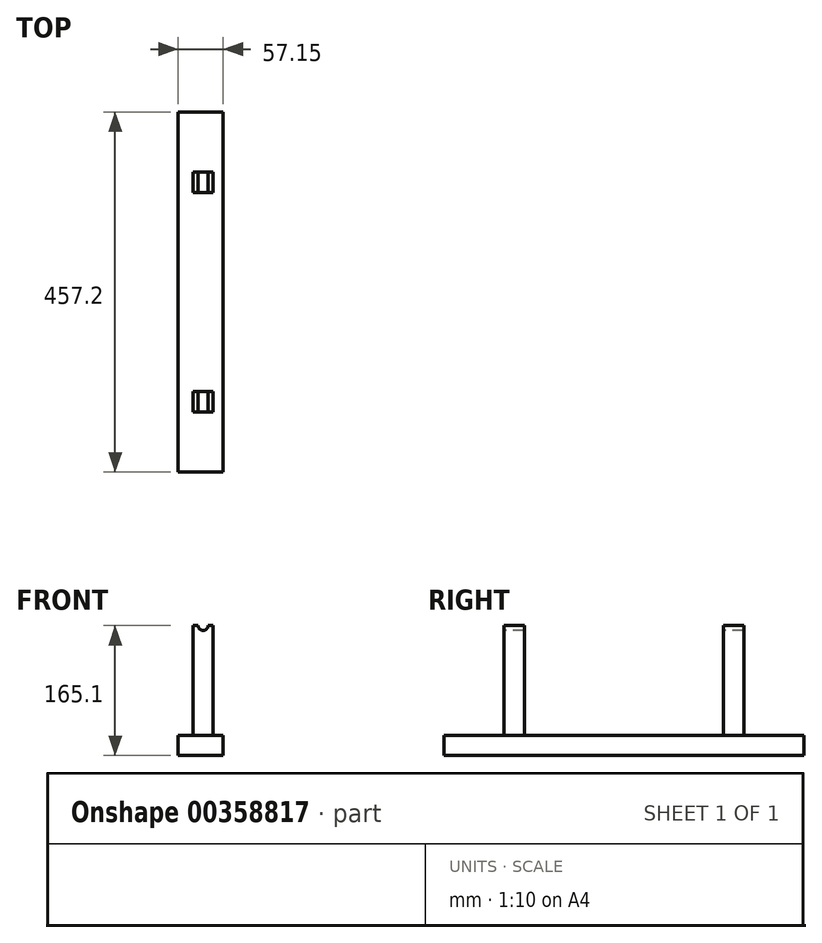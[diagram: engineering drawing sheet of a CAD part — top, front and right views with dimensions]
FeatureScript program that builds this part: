
annotation { "Feature Type Name" : "Feature", "Feature Type Description" : "" }
export const myFeature = defineFeature(function(context is Context, id is Id, definition is map)
    precondition{}
    {
        {
            var Q0;
            Q0=qCreatedBy(makeId("Right.planeOp"),FACE);
            var sketch = newSketch(context, id + "F0", { "sketchPlane" : qUnion([Q0])});
            skLineSegment(sketch, "E0.bottom", {"start": v(0, 0) * mm, "end": v(457.2, 0) * mm});
            skLineSegment(sketch, "E0.top", {"start": v(0, 25.4) * mm, "end": v(457.2, 25.4) * mm});
            skLineSegment(sketch, "E0.left", {"start": v(0, 0) * mm, "end": v(0, 25.4) * mm});
            skLineSegment(sketch, "E0.right", {"start": v(457.2, 0) * mm, "end": v(457.2, 25.4) * mm});
            skSolve(sketch);
        }
        {
            var Q0;
            Q0=qSketchRegion(id+"F0",true);
            extrude(context, id + "F1", {"entities" : qUnion([Q0]), "oppositeDirection" : true, "depth" : 203.2 * mm});
        }
        {
            var Q0;
            Q0=makeQuery(id+"F1.opExtrude","CAP_FACE",FACE,{"disambiguationData":[OSD([sQuery(id+"F0.wireOp",EDGE,"E0.bottom"),sQuery(id+"F0.wireOp",EDGE,"E0.top"),sQuery(id+"F0.wireOp",EDGE,"E0.left"),sQuery(id+"F0.wireOp",EDGE,"E0.right")])],"isStart":true});
            var sketch = newSketch(context, id + "F2", { "sketchPlane" : qUnion([Q0])});
            skLineSegment(sketch, "E1.bottom", {"start": v(76.2, 25.4) * mm, "end": v(102.38, 25.4) * mm});
            skLineSegment(sketch, "E1.top", {"start": v(76.2, 165.1) * mm, "end": v(102.38, 165.1) * mm});
            skLineSegment(sketch, "E1.left", {"start": v(76.2, 25.4) * mm, "end": v(76.2, 165.1) * mm});
            skLineSegment(sketch, "E1.right", {"start": v(102.38, 25.4) * mm, "end": v(102.38, 165.1) * mm});
            skLineSegment(sketch, "E2", {"start": v(228.6, 68.14) * mm, "end": v(228.6, -33.61) * mm});
            skPoint(sketch, "E2.startSnap0", {"position": v(228.6, 25.4) * mm});
            skLineSegment(sketch, "E3.MirrorCS", {"start": v(381, 25.4) * mm, "end": v(381, 165.1) * mm});
            skLineSegment(sketch, "E4.MirrorCS", {"start": v(381, 25.4) * mm, "end": v(354.82, 25.4) * mm});
            skLineSegment(sketch, "E5.MirrorCS", {"start": v(354.82, 25.4) * mm, "end": v(354.82, 165.1) * mm});
            skLineSegment(sketch, "E6.MirrorCS", {"start": v(381, 165.1) * mm, "end": v(354.82, 165.1) * mm});
            skSolve(sketch);
        }
        {
            var Q0;
            Q0=qSketchRegion(id+"F2",true);
            extrude(context, id + "F3", {"entities" : qUnion([Q0]), "oppositeDirection" : true, "depth" : 38.1 * mm});
        }
        {
            var Q0;
            Q0=makeQuery(id+"F3.opExtrude","SWEPT_FACE",FACE,{"disambiguationData":[OSD([sQuery(id+"F2.wireOp",EDGE,"E1.left")])]});
            var sketch = newSketch(context, id + "F4", { "sketchPlane" : qUnion([Q0])});
            skLineSegment(sketch, "E7.bottom", {"start": v(0, 25.4) * mm, "end": v(-12.7, 25.4) * mm});
            skLineSegment(sketch, "E7.top", {"start": v(0, 165.1) * mm, "end": v(-12.7, 165.1) * mm});
            skLineSegment(sketch, "E7.left", {"start": v(0, 25.4) * mm, "end": v(0, 165.1) * mm});
            skLineSegment(sketch, "E7.right", {"start": v(-12.7, 25.4) * mm, "end": v(-12.7, 165.1) * mm});
            skSolve(sketch);
        }
        {
            var Q0;
            Q0=qSketchRegion(id+"F4",true);
            extrude(context, id + "F5", {"entities" : qUnion([Q0]), "operationType" : NewBodyOperationType.REMOVE, "endBound" : BoundingType.THROUGH_ALL, "oppositeDirection" : true, "depth" : 25.4 * mm});
        }
        {
            var Q0;
            Q0=makeQuery(id+"F1.opExtrude","CAP_FACE",FACE,{"disambiguationData":[OSD([sQuery(id+"F0.wireOp",EDGE,"E0.bottom"),sQuery(id+"F0.wireOp",EDGE,"E0.top"),sQuery(id+"F0.wireOp",EDGE,"E0.left"),sQuery(id+"F0.wireOp",EDGE,"E0.right")])],"isStart":false});
            var sketch = newSketch(context, id + "F6", { "sketchPlane" : qUnion([Q0])});
            skLineSegment(sketch, "E8.bottom", {"start": v(-331.33, 25.4) * mm, "end": v(-299.58, 25.4) * mm});
            skLineSegment(sketch, "E8.top", {"start": v(-331.33, 177.8) * mm, "end": v(-299.58, 177.8) * mm});
            skLineSegment(sketch, "E8.left", {"start": v(-331.33, 25.4) * mm, "end": v(-331.33, 177.8) * mm});
            skLineSegment(sketch, "E8.right", {"start": v(-299.58, 25.4) * mm, "end": v(-299.58, 177.8) * mm});
            skLineSegment(sketch, "E9.bottom", {"start": v(-172.58, 25.4) * mm, "end": v(-140.83, 25.4) * mm});
            skLineSegment(sketch, "E9.top", {"start": v(-172.58, 177.8) * mm, "end": v(-140.83, 177.8) * mm});
            skLineSegment(sketch, "E9.left", {"start": v(-172.58, 25.4) * mm, "end": v(-172.58, 177.8) * mm});
            skLineSegment(sketch, "E9.right", {"start": v(-140.83, 25.4) * mm, "end": v(-140.83, 177.8) * mm});
            skSolve(sketch);
        }
        {
            var Q0;
            Q0=qSketchRegion(id+"F6",true);
            extrude(context, id + "F7", {"entities" : qUnion([Q0]), "operationType" : NewBodyOperationType.ADD, "oppositeDirection" : true, "depth" : 38.1 * mm});
        }
        {
            var Q0;
            Q0=makeQuery(id+"F7.opExtrude","SWEPT_FACE",FACE,{"disambiguationData":[OSD([sQuery(id+"F6.wireOp",EDGE,"E8.left")])]});
            var sketch = newSketch(context, id + "F8", { "sketchPlane" : qUnion([Q0])});
            skPoint(sketch, "E10", {"position": v(184.15, 165.1) * mm});
            skPoint(sketch, "E10.positionSnap0", {"position": v(184.15, 177.8) * mm});
            skCircle(sketch, "E11.cCircle", {"center": v(184.15, 165.1) * mm, "radius": 25.4 * mm, "construction": true});
            skLineSegment(sketch, "E11.0", {"start": v(169.49, 190.5) * mm, "end": v(198.81, 190.5) * mm});
            skLineSegment(sketch, "E11.1", {"start": v(198.81, 190.5) * mm, "end": v(213.48, 165.1) * mm});
            skLineSegment(sketch, "E11.2", {"start": v(213.48, 165.1) * mm, "end": v(198.81, 139.7) * mm});
            skLineSegment(sketch, "E11.3", {"start": v(198.81, 139.7) * mm, "end": v(169.49, 139.7) * mm});
            skLineSegment(sketch, "E11.4", {"start": v(169.49, 139.7) * mm, "end": v(154.82, 165.1) * mm});
            skLineSegment(sketch, "E11.5", {"start": v(154.82, 165.1) * mm, "end": v(169.49, 190.5) * mm});
            skPoint(sketch, "E11.0.midPoint", {"position": v(184.15, 190.5) * mm});
            skSolve(sketch);
        }
        {
            var Q0;
            Q0=qSketchRegion(id+"F8",true);
            extrude(context, id + "F9", {"entities" : qUnion([Q0]), "operationType" : NewBodyOperationType.ADD, "oppositeDirection" : true, "depth" : 196.85 * mm, "hasSecondDirection" : true, "secondDirectionOppositeDirection" : false, "secondDirectionDepth" : 6.35 * mm});
        }
        {
            var Q0;
            Q0=makeQuery(id+"F7.boolean.opBoolean","MERGE",FACE,{"derivedFrom":[makeQuery(id+"F1.opExtrude","CAP_FACE",FACE,{"disambiguationData":[OSD([sQuery(id+"F0.wireOp",EDGE,"E0.bottom"),sQuery(id+"F0.wireOp",EDGE,"E0.top"),sQuery(id+"F0.wireOp",EDGE,"E0.left"),sQuery(id+"F0.wireOp",EDGE,"E0.right")])],"isStart":false}),makeQuery(id+"F7.opExtrude","CAP_FACE",FACE,{"disambiguationData":[OSD([sQuery(id+"F6.wireOp",EDGE,"E8.bottom"),sQuery(id+"F6.wireOp",EDGE,"E8.top"),sQuery(id+"F6.wireOp",EDGE,"E8.left"),sQuery(id+"F6.wireOp",EDGE,"E8.right")])],"isStart":true}),makeQuery(id+"F7.opExtrude","CAP_FACE",FACE,{"disambiguationData":[OSD([sQuery(id+"F6.wireOp",EDGE,"E9.bottom"),sQuery(id+"F6.wireOp",EDGE,"E9.top"),sQuery(id+"F6.wireOp",EDGE,"E9.left"),sQuery(id+"F6.wireOp",EDGE,"E9.right")])],"isStart":true})]});
            var sketch = newSketch(context, id + "F10", { "sketchPlane" : qUnion([Q0])});
            skLineSegment(sketch, "E12", {"start": v(-299.58, 139.7) * mm, "end": v(-299.58, 190.5) * mm});
            skLineSegment(sketch, "E13", {"start": v(-299.58, 190.5) * mm, "end": v(-173.69, 190.5) * mm});
            skLineSegment(sketch, "E14", {"start": v(-173.69, 190.5) * mm, "end": v(-172.58, 139.7) * mm});
            skLineSegment(sketch, "E15", {"start": v(-172.58, 139.7) * mm, "end": v(-299.58, 139.7) * mm});
            skSolve(sketch);
        }
        {
            var Q0;
            Q0=qSketchRegion(id+"F10",true);
            extrude(context, id + "F11", {"entities" : qUnion([Q0]), "operationType" : NewBodyOperationType.REMOVE, "oppositeDirection" : true, "depth" : 50.8 * mm});
        }
        {
            var Q0;
            Q0=makeQuery(id+"F11.boolean.opBoolean","MERGE",FACE,{"derivedFrom":[makeQuery(id+"F7.opExtrude","SWEPT_FACE",FACE,{"disambiguationData":[OSD([sQuery(id+"F6.wireOp",EDGE,"E8.right")])]}),makeQuery(id+"F11.opExtrude","SWEPT_FACE",FACE,{"disambiguationData":[OSD([sQuery(id+"F10.wireOp",EDGE,"E12")])]})]});
            var sketch = newSketch(context, id + "F12", { "sketchPlane" : qUnion([Q0])});
            skPoint(sketch, "E16", {"position": v(-184.15, 165.1) * mm});
            skPoint(sketch, "E16.positionSnap0", {"position": v(-184.15, 190.5) * mm});
            skCircle(sketch, "E17", {"center": v(-184.15, 165.1) * mm, "radius": 22.23 * mm});
            skSolve(sketch);
        }
        {
            var Q0;
            Q0=qSketchRegion(id+"F12",true);
            extrude(context, id + "F13", {"entities" : qUnion([Q0]), "operationType" : NewBodyOperationType.REMOVE, "oppositeDirection" : true, "depth" : 12.7 * mm, "hasSecondDirection" : true, "secondDirectionOppositeDirection" : false, "secondDirectionDepth" : 139.7 * mm});
        }
        {
            var Q0;
            Q0=makeQuery(id+"F9.opExtrude","CAP_FACE",FACE,{"disambiguationData":[OSD([sQuery(id+"F8.wireOp",EDGE,"E11.0"),sQuery(id+"F8.wireOp",EDGE,"E11.1"),sQuery(id+"F8.wireOp",EDGE,"E11.2"),sQuery(id+"F8.wireOp",EDGE,"E11.3"),sQuery(id+"F8.wireOp",EDGE,"E11.4"),sQuery(id+"F8.wireOp",EDGE,"E11.5")])],"isStart":false});
            var sketch = newSketch(context, id + "F14", { "sketchPlane" : qUnion([Q0])});
            skPoint(sketch, "E18", {"position": v(-184.15, 165.1) * mm});
            skPoint(sketch, "E18.positionSnap0", {"position": v(-184.15, 190.5) * mm});
            skCircle(sketch, "E19", {"center": v(-184.15, 165.1) * mm, "radius": 19.05 * mm});
            skSolve(sketch);
        }
        {
            var Q0;
            Q0=qSketchRegion(id+"F14",true);
            extrude(context, id + "F15", {"entities" : qUnion([Q0]), "operationType" : NewBodyOperationType.REMOVE, "oppositeDirection" : true, "depth" : 6.35 * mm});
        }
        {
            var Q0;
            Q0=makeQuery(id+"F9.opExtrude","CAP_FACE",FACE,{"disambiguationData":[OSD([sQuery(id+"F8.wireOp",EDGE,"E11.0"),sQuery(id+"F8.wireOp",EDGE,"E11.1"),sQuery(id+"F8.wireOp",EDGE,"E11.2"),sQuery(id+"F8.wireOp",EDGE,"E11.3"),sQuery(id+"F8.wireOp",EDGE,"E11.4"),sQuery(id+"F8.wireOp",EDGE,"E11.5")])],"isStart":true});
            var sketch = newSketch(context, id + "F16", { "sketchPlane" : qUnion([Q0])});
            skPoint(sketch, "E20", {"position": v(184.15, 165.1) * mm});
            skPoint(sketch, "E20.positionSnap0", {"position": v(184.15, 190.5) * mm});
            skCircle(sketch, "E21", {"center": v(184.15, 165.1) * mm, "radius": 19.05 * mm});
            skSolve(sketch);
        }
        {
            var Q0;
            Q0=qSketchRegion(id+"F16",true);
            extrude(context, id + "F17", {"entities" : qUnion([Q0]), "operationType" : NewBodyOperationType.REMOVE, "oppositeDirection" : true, "depth" : 6.35 * mm});
        }
        {
            var Q0;
            Q0=makeQuery(id+"F11.boolean.opBoolean","MERGE",FACE,{"derivedFrom":[makeQuery(id+"F7.opExtrude","SWEPT_FACE",FACE,{"disambiguationData":[OSD([sQuery(id+"F6.wireOp",EDGE,"E8.right")])]}),makeQuery(id+"F11.opExtrude","SWEPT_FACE",FACE,{"disambiguationData":[OSD([sQuery(id+"F10.wireOp",EDGE,"E12")])]})]});
            cPlane(context, id + "F18", {"entities" : qUnion([Q0]), "cplaneType" : CPlaneType.OFFSET, "offset" : 6.35 * mm, "width" : 152.4 * mm, "height" : 152.4 * mm});
        }
        {
            var Q0;
            Q0=makeQuery(id+"F13.boolean.opBoolean","COPY",FACE,{"derivedFrom":makeQuery(id+"F13.opExtrude","CAP_FACE",FACE,{"disambiguationData":[OSD([sQuery(id+"F12.wireOp",EDGE,"E17")])],"isStart":true})});
            var sketch = newSketch(context, id + "F19", { "sketchPlane" : qUnion([Q0])});
            skCircle(sketch, "E22", {"center": v(184.15, 165.1) * mm, "radius": 12.7 * mm});
            skSolve(sketch);
        }
        {
            var Q0;
            Q0=qSketchRegion(id+"F19",true);
            extrude(context, id + "F20", {"entities" : qUnion([Q0]), "depth" : 190.5 * mm, "hasSecondDirection" : true, "secondDirectionOppositeDirection" : true, "secondDirectionDepth" : 38.1 * mm});
        }
        {
            var Q0;
            Q0=qCreatedBy(id+"F18.planeOp",FACE);
            var sketch = newSketch(context, id + "F21", { "sketchPlane" : qUnion([Q0])});
            skCircle(sketch, "E23", {"center": v(-184.15, 165.1) * mm, "radius": 19.05 * mm});
            skLineSegment(sketch, "E24", {"start": v(-184.15, 184.15) * mm, "end": v(-75.32, 266.65) * mm});
            skLineSegment(sketch, "E25", {"start": v(-184.15, 184.15) * mm, "end": v(-184.15, 165.1) * mm});
            skPoint(sketch, "E26", {"position": v(-62.62, 266.65) * mm});
            skPoint(sketch, "E27", {"position": v(-62.62, 165.05) * mm});
            skLineSegment(sketch, "E28", {"start": v(-75.32, 266.65) * mm, "end": v(-62.62, 266.65) * mm});
            skLineSegment(sketch, "E29", {"start": v(-62.62, 165.05) * mm, "end": v(-62.62, 266.65) * mm});
            skLineSegment(sketch, "E30", {"start": v(-62.62, 165.05) * mm, "end": v(-184.15, 165.1) * mm});
            skLineSegment(sketch, "E31.MirrorCS", {"start": v(-184.17, 146.05) * mm, "end": v(-184.15, 165.1) * mm});
            skLineSegment(sketch, "E32.MirrorCS", {"start": v(-184.17, 146.05) * mm, "end": v(-75.4, 63.46) * mm});
            skLineSegment(sketch, "E33.MirrorCS", {"start": v(-62.62, 165.05) * mm, "end": v(-62.7, 63.45) * mm});
            skLineSegment(sketch, "E34.MirrorCS", {"start": v(-75.4, 63.46) * mm, "end": v(-62.7, 63.45) * mm});
            skSolve(sketch);
        }
        {
            var Q0;
            Q0=qSketchRegion(id+"F21",true);
            extrude(context, id + "F22", {"entities" : qUnion([Q0]), "depth" : 114.3 * mm});
        }
        {
            var Q0;
            Q0=makeQuery(id+"F22.opExtrude","SWEPT_FACE",FACE,{"disambiguationData":[OSD([sQuery(id+"F21.wireOp",EDGE,"E28")])]});
            var sketch = newSketch(context, id + "F23", { "sketchPlane" : qUnion([Q0])});
            skPoint(sketch, "E35", {"position": v(-72.14, 274.18) * mm});
            skPoint(sketch, "E36", {"position": v(-176.84, 280.53) * mm});
            skPoint(sketch, "E37", {"position": v(-72.14, 197.98) * mm});
            skPoint(sketch, "E38", {"position": v(-176.84, 191.63) * mm});
            skLineSegment(sketch, "E39", {"start": v(-72.14, 274.18) * mm, "end": v(-176.84, 280.53) * mm});
            skLineSegment(sketch, "E40", {"start": v(-176.84, 280.53) * mm, "end": v(-176.84, 191.63) * mm});
            skLineSegment(sketch, "E41", {"start": v(-176.84, 191.63) * mm, "end": v(-72.14, 197.98) * mm});
            skLineSegment(sketch, "E42", {"start": v(-72.14, 274.18) * mm, "end": v(-72.14, 197.98) * mm});
            skSolve(sketch);
        }
        {
            var Q0;
            Q0=qSketchRegion(id+"F23",true);
            extrude(context, id + "F24", {"entities" : qUnion([Q0]), "operationType" : NewBodyOperationType.REMOVE, "oppositeDirection" : true, "depth" : 209.55 * mm});
        }
        {
            var Q0;
            Q0=makeQuery(id+"F22.opExtrude","SWEPT_FACE",FACE,{"disambiguationData":[OSD([sQuery(id+"F21.wireOp",EDGE,"E28")])]});
            var sketch = newSketch(context, id + "F25", { "sketchPlane" : qUnion([Q0])});
            skPoint(sketch, "E43.positionSnap0", {"position": v(-68.97, 293.23) * mm});
            skPoint(sketch, "E44.positionSnap0", {"position": v(-68.97, 178.93) * mm});
            skLineSegment(sketch, "E45", {"start": v(-72.14, 261.48) * mm, "end": v(-62.62, 261.48) * mm});
            skLineSegment(sketch, "E46", {"start": v(-62.62, 261.48) * mm, "end": v(-62.62, 210.68) * mm});
            skLineSegment(sketch, "E47", {"start": v(-62.62, 210.68) * mm, "end": v(-72.14, 210.68) * mm});
            skLineSegment(sketch, "E48", {"start": v(-72.14, 210.68) * mm, "end": v(-72.14, 261.48) * mm});
            skSolve(sketch);
        }
        {
            var Q0;
            Q0=qSketchRegion(id+"F25",true);
            extrude(context, id + "F26", {"entities" : qUnion([Q0]), "operationType" : NewBodyOperationType.REMOVE, "oppositeDirection" : true, "depth" : 209.55 * mm});
        }
        {
            var Q0;
            Q0=makeQuery(id+"F26.boolean.opBoolean","COPY",FACE,{"derivedFrom":makeQuery(id+"F26.opExtrude","SWEPT_FACE",FACE,{"disambiguationData":[OSD([sQuery(id+"F25.wireOp",EDGE,"E45")])]})});
            var sketch = newSketch(context, id + "F27", { "sketchPlane" : qUnion([Q0])});
            skPoint(sketch, "E49", {"position": v(-62.62, 184.1) * mm});
            skPoint(sketch, "E50", {"position": v(-72.14, 184.1) * mm});
            skPoint(sketch, "E51", {"position": v(-62.62, 235.78) * mm});
            skPoint(sketch, "E52", {"position": v(-72.14, 228.55) * mm});
            skPoint(sketch, "E53", {"position": v(-62.64, 146) * mm});
            skPoint(sketch, "E54", {"position": v(-72.14, 146) * mm});
            skPoint(sketch, "E55", {"position": v(-62.68, 94.36) * mm});
            skPoint(sketch, "E56", {"position": v(-72.14, 101.55) * mm});
            skLineSegment(sketch, "E57", {"start": v(-72.14, 228.55) * mm, "end": v(-62.62, 235.78) * mm});
            skLineSegment(sketch, "E58", {"start": v(-72.14, 101.55) * mm, "end": v(-62.68, 94.36) * mm});
            skPoint(sketch, "E59", {"position": v(-62.7, 81.66) * mm});
            skPoint(sketch, "E60", {"position": v(-72.14, 88.85) * mm});
            skPoint(sketch, "E61", {"position": v(-72.14, 241.25) * mm});
            skPoint(sketch, "E62", {"position": v(-62.62, 248.48) * mm});
            skLineSegment(sketch, "E63", {"start": v(-72.14, 184.1) * mm, "end": v(-62.62, 184.1) * mm});
            skLineSegment(sketch, "E64", {"start": v(-72.14, 146) * mm, "end": v(-62.64, 146) * mm});
            skLineSegment(sketch, "E65", {"start": v(-62.62, 248.48) * mm, "end": v(-62.62, 235.78) * mm});
            skLineSegment(sketch, "E66", {"start": v(-72.14, 241.25) * mm, "end": v(-62.62, 248.48) * mm});
            skLineSegment(sketch, "E67", {"start": v(-72.14, 241.25) * mm, "end": v(-72.14, 228.55) * mm});
            skLineSegment(sketch, "E68", {"start": v(-72.14, 88.85) * mm, "end": v(-72.14, 101.55) * mm});
            skLineSegment(sketch, "E69", {"start": v(-62.7, 81.66) * mm, "end": v(-62.68, 94.36) * mm});
            skLineSegment(sketch, "E70", {"start": v(-62.7, 81.66) * mm, "end": v(-72.14, 88.85) * mm});
            skLineSegment(sketch, "E71", {"start": v(-62.64, 146) * mm, "end": v(-62.62, 184.1) * mm});
            skLineSegment(sketch, "E72", {"start": v(-72.14, 184.1) * mm, "end": v(-72.14, 146) * mm});
            skPoint(sketch, "E73", {"position": v(-62.62, 165.05) * mm});
            skSolve(sketch);
        }
        {
            var Q0;
            Q0=qSketchRegion(id+"F27",true);
            extrude(context, id + "F28", {"entities" : qUnion([Q0]), "operationType" : NewBodyOperationType.REMOVE, "oppositeDirection" : true, "depth" : 12.7 * mm, "hasSecondDirection" : true, "secondDirectionOppositeDirection" : false, "secondDirectionDepth" : 63.5 * mm});
        }
        {
            var Q0;
            Q0=makeQuery(id+"F3.opExtrude","SWEPT_FACE",FACE,{"disambiguationData":[OSD([sQuery(id+"F2.wireOp",EDGE,"E1.left")])]});
            var sketch = newSketch(context, id + "F29", { "sketchPlane" : qUnion([Q0])});
            skCircle(sketch, "E74", {"center": v(-25.4, 165.1) * mm, "radius": 6.35 * mm});
            skSolve(sketch);
        }
        {
            var Q0;
            Q0=qSketchRegion(id+"F29",true);
            extrude(context, id + "F30", {"entities" : qUnion([Q0]), "operationType" : NewBodyOperationType.REMOVE, "oppositeDirection" : true, "depth" : 406.4 * mm});
        }
        {
            var Q0;
            Q0=makeQuery(id+"F1.opExtrude","SWEPT_FACE",FACE,{"disambiguationData":[OSD([sQuery(id+"F0.wireOp",EDGE,"E0.left")])]});
            var sketch = newSketch(context, id + "F31", { "sketchPlane" : qUnion([Q0])});
            skPoint(sketch, "E75", {"position": v(-57.15, 0) * mm});
            skLineSegment(sketch, "E76.bottom", {"start": v(-57.15, 0) * mm, "end": v(-234.95, 0) * mm});
            skLineSegment(sketch, "E76.top", {"start": v(-57.15, 271.2) * mm, "end": v(-234.95, 271.2) * mm});
            skLineSegment(sketch, "E76.left", {"start": v(-57.15, 0) * mm, "end": v(-57.15, 271.2) * mm});
            skLineSegment(sketch, "E76.right", {"start": v(-234.95, 0) * mm, "end": v(-234.95, 271.2) * mm});
            skSolve(sketch);
        }
        {
            var Q0;
            Q0 = qSketchRegion(id + "F31", true);
            extrude(context, id + "F32", {"entities" : qUnion([Q0]), "operationType" : NewBodyOperationType.REMOVE, "endBound" : BoundingType.THROUGH_ALL, "oppositeDirection" : true, "depth" : 25.4 * mm});
        }
    });
